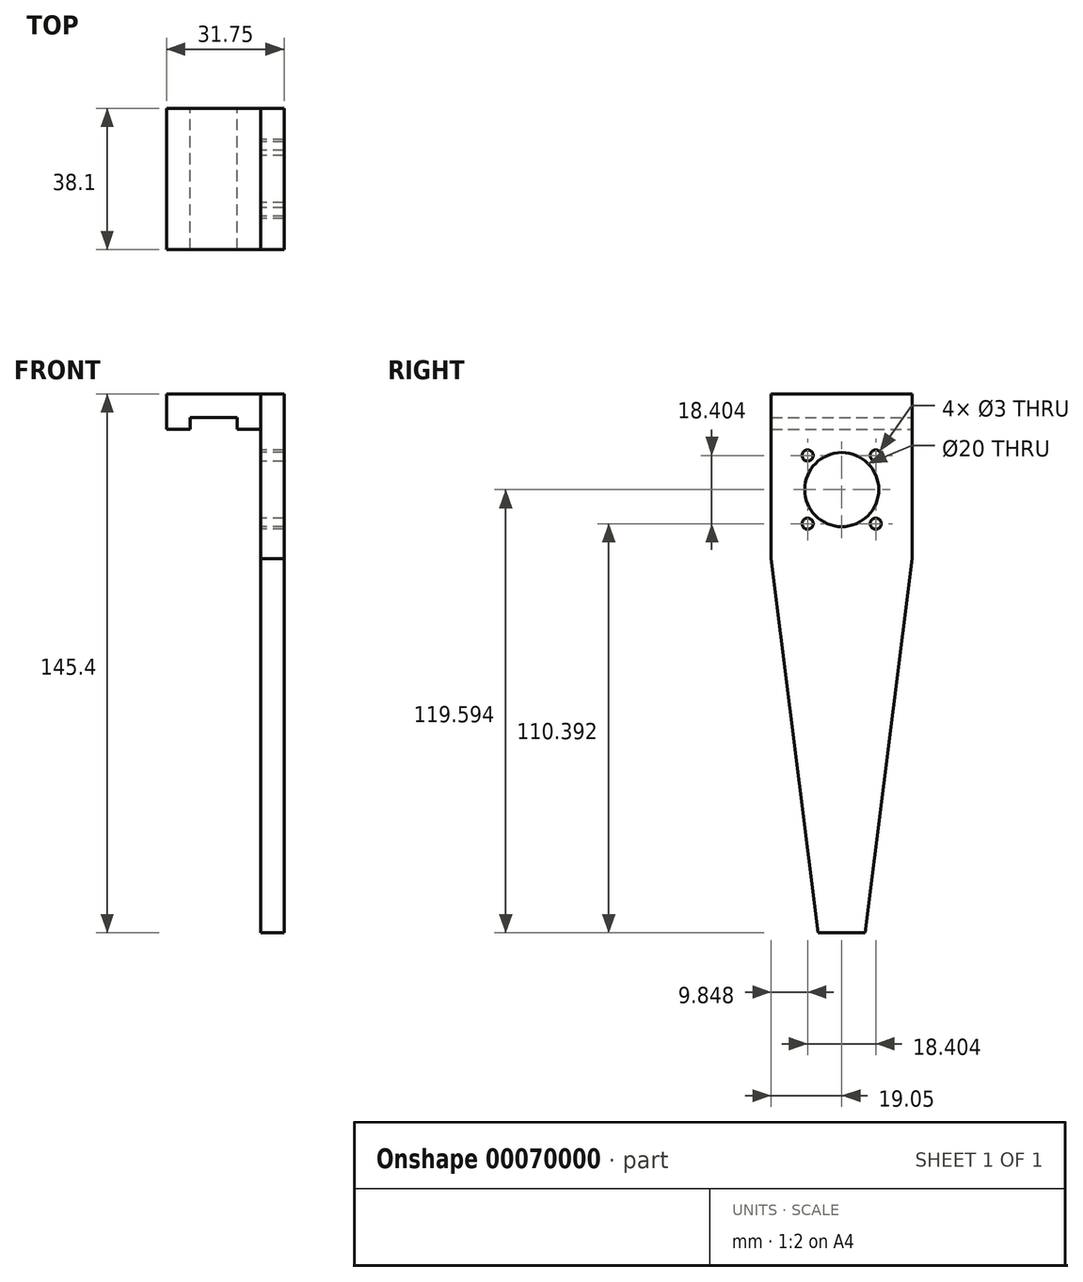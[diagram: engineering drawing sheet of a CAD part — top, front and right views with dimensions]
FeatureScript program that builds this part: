
annotation { "Feature Type Name" : "Feature", "Feature Type Description" : "" }
export const myFeature = defineFeature(function(context is Context, id is Id, definition is map)
    precondition{}
    {
        {
            var Q0;
            Q0=qCreatedBy(makeId("Front.planeOp"),FACE);
            var sketch = newSketch(context, id + "F0", { "sketchPlane" : qUnion([Q0])});
            skLineSegment(sketch, "E0.bottom", {"start": v(-25.4, 0) * mm, "end": v(0, 0) * mm});
            skLineSegment(sketch, "E0.top", {"start": v(-25.4, -9.52) * mm, "end": v(-19.05, -9.52) * mm});
            skLineSegment(sketch, "E0.left", {"start": v(-25.4, 0) * mm, "end": v(-25.4, -9.53) * mm});
            skLineSegment(sketch, "E0.right", {"start": v(0, 0) * mm, "end": v(0, -9.53) * mm});
            skLineSegment(sketch, "E1", {"start": v(-19.05, -9.52) * mm, "end": v(-19.05, -6.35) * mm});
            skLineSegment(sketch, "E2", {"start": v(-19.05, -6.35) * mm, "end": v(-6.35, -6.35) * mm});
            skLineSegment(sketch, "E3", {"start": v(-6.35, -6.35) * mm, "end": v(-6.35, -9.53) * mm});
            skLineSegment(sketch, "E4.trimOffspring", {"start": v(-6.35, -9.52) * mm, "end": v(0, -9.52) * mm});
            skSolve(sketch);
        }
        {
            var Q0;
            Q0 = qSketchRegion(id + "F0", true);
            extrude(context, id + "F1", {"entities" : qUnion([Q0]), "depth" : 38.1 * mm});
        }
        {
            var Q0;
            Q0=qCreatedBy(makeId("Right.planeOp"),FACE);
            var sketch = newSketch(context, id + "F2", { "sketchPlane" : qUnion([Q0])});
            skPoint(sketch, "E5.center", {"position": v(-19.05, -25.8) * mm});
            skCircle(sketch, "E6", {"center": v(-19.05, -25.8) * mm, "radius": 10 * mm});
            skCircle(sketch, "E7", {"center": v(-28.25, -16.6) * mm, "radius": 1.5 * mm});
            skCircle(sketch, "E5.1.0", {"center": v(-28.25, -35) * mm, "radius": 1.5 * mm});
            skCircle(sketch, "E5.2.0", {"center": v(-9.85, -35) * mm, "radius": 1.5 * mm});
            skCircle(sketch, "E5.3.0", {"center": v(-9.85, -16.6) * mm, "radius": 1.5 * mm});
            skCircle(sketch, "E8", {"center": v(-19.05, -25.8) * mm, "radius": 13 * mm, "construction": true});
            skLineSegment(sketch, "E9.bottom", {"start": v(-12.7, -120) * mm, "end": v(-25.4, -120) * mm, "construction": true});
            skLineSegment(sketch, "E9.top", {"start": v(-12.7, -145.4) * mm, "end": v(-25.4, -145.4) * mm});
            skLineSegment(sketch, "E9.left", {"start": v(-12.7, -120) * mm, "end": v(-12.7, -145.4) * mm, "construction": true});
            skLineSegment(sketch, "E9.right", {"start": v(-25.4, -120) * mm, "end": v(-25.4, -145.4) * mm, "construction": true});
            skLineSegment(sketch, "E10", {"start": v(-38.1, 0) * mm, "end": v(0, 0) * mm});
            skLineSegment(sketch, "E11", {"start": v(0, 0) * mm, "end": v(0, -44.45) * mm});
            skLineSegment(sketch, "E12", {"start": v(-38.1, 0) * mm, "end": v(-38.1, -44.45) * mm});
            skLineSegment(sketch, "E13", {"start": v(0, -44.45) * mm, "end": v(-12.7, -145.4) * mm});
            skLineSegment(sketch, "E14", {"start": v(-38.1, -44.45) * mm, "end": v(-25.4, -145.4) * mm});
            skSolve(sketch);
        }
        {
            var Q0;
            Q0 = qSketchRegion(id + "F2", true);
            extrude(context, id + "F3", {"entities" : qUnion([Q0]), "depth" : 6.35 * mm});
        }
    });
